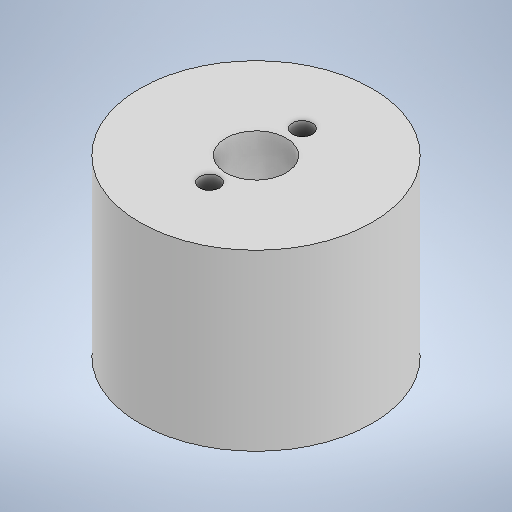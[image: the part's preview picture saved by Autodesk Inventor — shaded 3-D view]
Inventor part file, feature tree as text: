
AUTODESK INVENTOR PART (.ipt)
format: ipt  version: 2025.2 (Build 292293000, 293)  size: 218,112 bytes
history: native  units: in
note: dims shown in document units (in); Inventor stores cm internally (conversion verified against a paired STEP export)
features: extrude x3, sketch x3
ambient origin geometry x8: Origin, YZ Plane, XZ Plane, XY Plane, X Axis, Y Axis, Z Axis, Center Point
bodies: Solid1 (feature_tree)
feature tree (6):
  extrude  "Extrusion1"  Depth=0.26in
  extrude  "Extrusion2"  Depth=0.2in
  extrude  "Extrusion3"  Depth=0.075in
  sketch  "Sketch1"  dims[d0=1.0in d1=0.26in]
  sketch  "Sketch2"  dims[d2=0.75in d3=0.0in d4=0.2in]
  sketch  "Sketch3"  dims[d5=0.2in d6=0.086in d7=0.086in d8=0.175in d9=0.0in d10=0.2in d11=0.4in d12=0.075in d13=0.0in d14=0.086in d15=0.086in]
